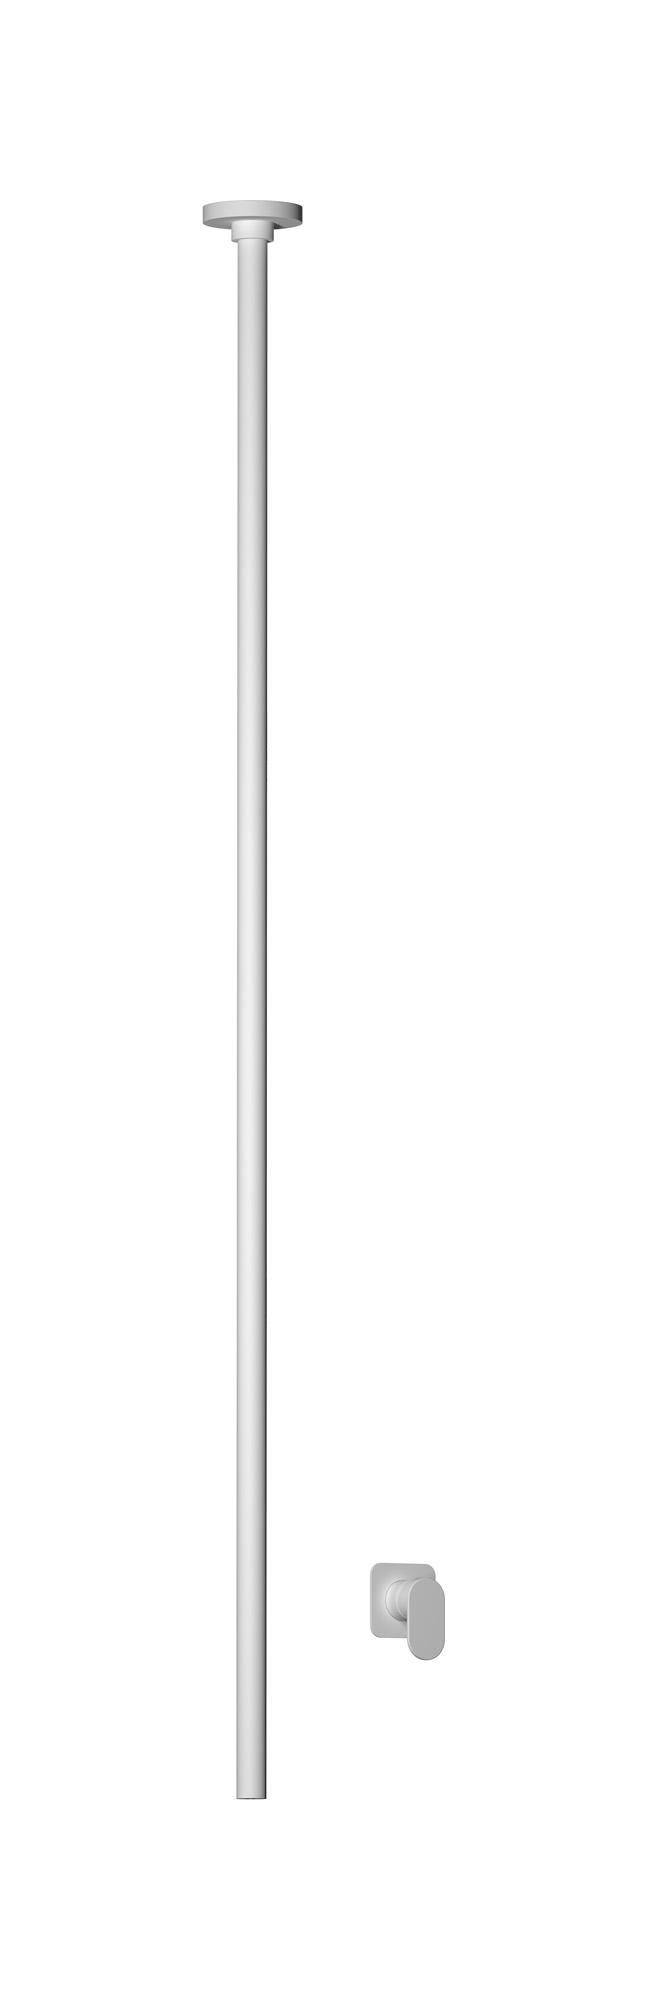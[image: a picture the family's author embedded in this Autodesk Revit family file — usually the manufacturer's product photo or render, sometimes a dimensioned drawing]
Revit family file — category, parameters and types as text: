
# Revit family: LM210
name_source: partatom
category: Apparecchi idraulici
units: mm (PartAtom-declared; Revit-internal decimal feet)

## family parameters
Basato su piano di lavoro = No
Condiviso = No
Mantieni orientamento annotazione = No
Numero OmniClass = 23.45.55.17
Punto di calcolo locali = No
Quota connettore circolare = Usa diametro
Sempre verticale = Sì
Taglio con vuoti quando caricato = No
Tipo di parte = Normale
Titolo OmniClass = Mixing Faucets

## types (5) — shared parameters
Cold water inlet = 10 mm  [stored 0.0328084 ft]
Commenti sul tipo = Wall mixer
Connessione CW = No
Connessione HW = No
Connessione di scarico = No
Connessione di ventilazione = No
Descrizione = Ceiling spout with wall mounted mixer
Hot water inlet = 10 mm  [stored 0.0328084 ft]
Produttore = IB Rubinetterie S.p.A.
URL = https://www.weareib.it
zero-valued in all types: Prospetto di default

## per-type parameters (varying)
| type | Finishes surface | Immagine tipo | Modello |
| Chrome | IB_Chrome | LM210CC.jpg | LM210CC |
| Brushed nickel | IB_Brushed nickel | LM210SS.jpg | LM210SS |
| Matt white | IB_matt white | LM210BO.jpg | LM210BO |
| Matt black | IB_matt black | LM210NP.jpg | LM210NP |
| Natural brass | IB_Brass | LM210ON.jpg | LM210ON |

note: [stored X ft] marks values corroborated as IEEE doubles in the binary element streams (Revit-internal decimal feet)
